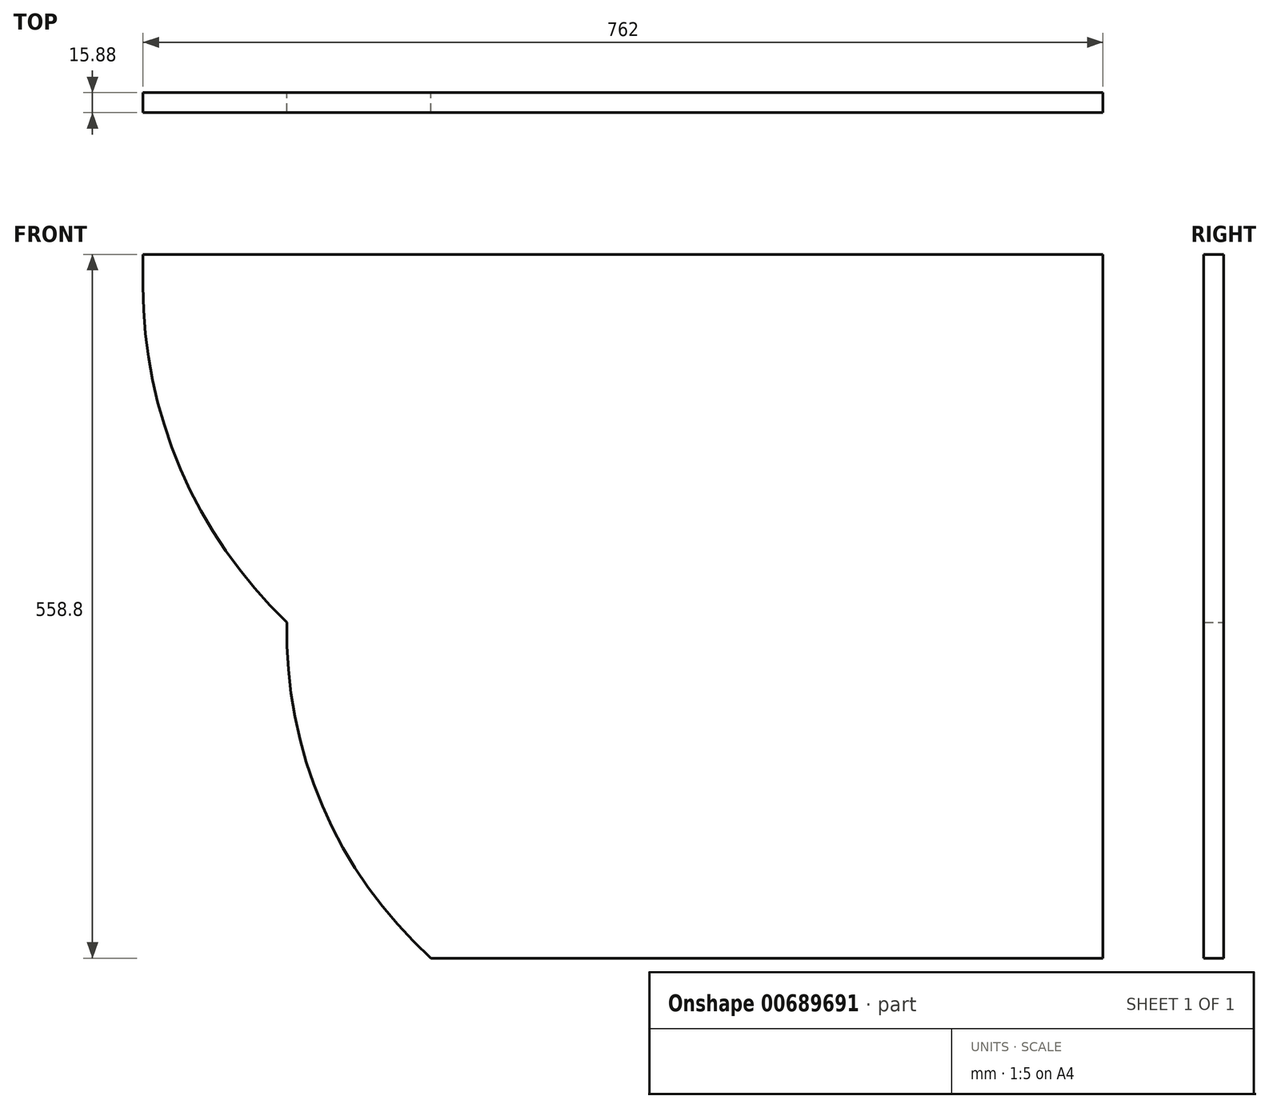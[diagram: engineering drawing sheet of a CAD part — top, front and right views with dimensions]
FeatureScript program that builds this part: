
annotation { "Feature Type Name" : "Feature", "Feature Type Description" : "" }
export const myFeature = defineFeature(function(context is Context, id is Id, definition is map)
    precondition{}
    {
        {
            var Q0;
            Q0=qCreatedBy(makeId("Front.planeOp"),FACE);
            var sketch = newSketch(context, id + "F0", { "sketchPlane" : qUnion([Q0])});
            skLineSegment(sketch, "E0", {"start": v(-59.44, 25.4) * mm, "end": v(702.56, 25.4) * mm});
            skLineSegment(sketch, "E1", {"start": v(702.56, 25.4) * mm, "end": v(702.56, -533.4) * mm});
            skLineSegment(sketch, "E2", {"start": v(702.56, -533.4) * mm, "end": v(169.16, -533.4) * mm});
            skLineSegment(sketch, "E3", {"start": v(-59.44, 25.4) * mm, "end": v(-59.44, 0) * mm});
            skArc(sketch, "E4", {"start": v(-59.44, 0) * mm, "mid": v(-29.66, -145.08) * mm, "end": v(54.86, -266.7) * mm});
            skArc(sketch, "E5", {"start": v(54.86, -266.7) * mm, "mid": v(82.96, -412.5) * mm, "end": v(169.16, -533.4) * mm});
            skSolve(sketch);
        }
        {
            var Q0;
            Q0=makeQuery(id+"F0.imprint","IMPRINT",FACE,{"disambiguationData":[TD([[makeQuery(id+"F0.imprint","IMPRINT",EDGE,{"derivedFrom":sQuery(id+"F0.wireOp",EDGE,"E0")}),-1.0]])]});
            extrude(context, id + "F1", {"entities" : qUnion([Q0]), "depth" : 15.88 * mm, "offsetDistance" : 25.4 * mm});
        }
    });
